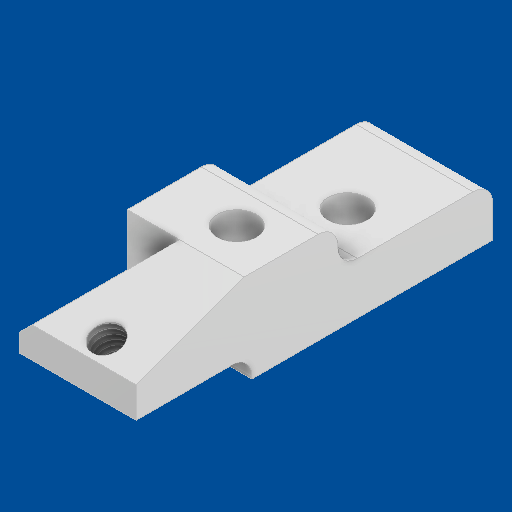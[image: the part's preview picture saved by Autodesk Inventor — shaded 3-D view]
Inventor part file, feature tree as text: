
AUTODESK INVENTOR PART (.ipt)
format: ipt  version: 2025 (Build 290162000, 162)  size: 243,200 bytes
history: native  units: in
note: dims shown in document units (in); Inventor stores cm internally (conversion verified against a paired STEP export)
features: move_body x12, direct_edit x9, sketch x2, hole x2, other x2, fillet x1
ambient origin geometry x8: Origin, YZ Plane, XZ Plane, XY Plane, X Axis, Y Axis, Z Axis, Center Point
bodies: Solid1 (feature_tree), Body10 (feature_tree)
feature tree (28):
  direct_edit  "Direct Edit1"
  direct_edit  "Direct Edit2"
  sketch  "Sketch1"  dims[d0=0.0in d1=0.0in d2=0.0254in d3=0.0394in]
  direct_edit  "Direct Edit3"
  hole  "Hole1"  [1 undecoded]
  hole  "Hole2"  [1 undecoded]
  fillet  "Fillet1"  [1 undecoded]
  direct_edit  "Direct Edit4"
  direct_edit  "Direct Edit5"
  direct_edit  "Direct Edit6"
  direct_edit  "Direct Edit7"
  direct_edit  "Direct Edit8"
  direct_edit  "Direct Edit9"
  sketch  "Sketch2"  dims[d4=0.0394in d5=0.0968in d6=2.3622in d7=0.1575in d8=0.0787in d9=90.0deg d10=3.1811in d11=0.8108in d12=0.0968in d13=2.3622in d14=0.1575in d15=0.0787in d16=90.0deg d17=3.1811in d18=0.8108in d19=0.063in d20=0.0in d21=0.0in d22=-0.0008in d23=0.0in d24=0.0in d25=-0.0035in d26=0.0in d27=0.0in d28=-0.0047in d29=0.0in d30=0.0in d31=-0.0047in d32=0.0in d33=0.0in d34=-0.0047in d36=0.0051in d37=-0.002in d38=0.0in d39=0.0in d40=0.0in d41=-0.0043in d42=0.0in d43=-0.0004in d44=0.0in d45=0.0in d46=-0.002in d47=0.0in d48=0.0in d49=0.0in d50=0.0in d51=-0.0008in d52=0.0in d53=0.0in d54=0.0008in]
  move_body  "Move1"
  other  "Size1"
  other  "Size2"
  move_body  "Move2"
  move_body  "Move3"
  move_body  "Move4"
  move_body  "Move5"
  move_body  "Move6"
  move_body  "Move7"
  move_body  "Move8"
  move_body  "Move9"
  move_body  "Move10"
  move_body  "Move11"
  move_body  "Move12"
note: 3 required parameter values undecoded (feature->parameter linkage not recoverable at this tier; creation-order binding heuristic only, values carry confidence <= 0.55)
